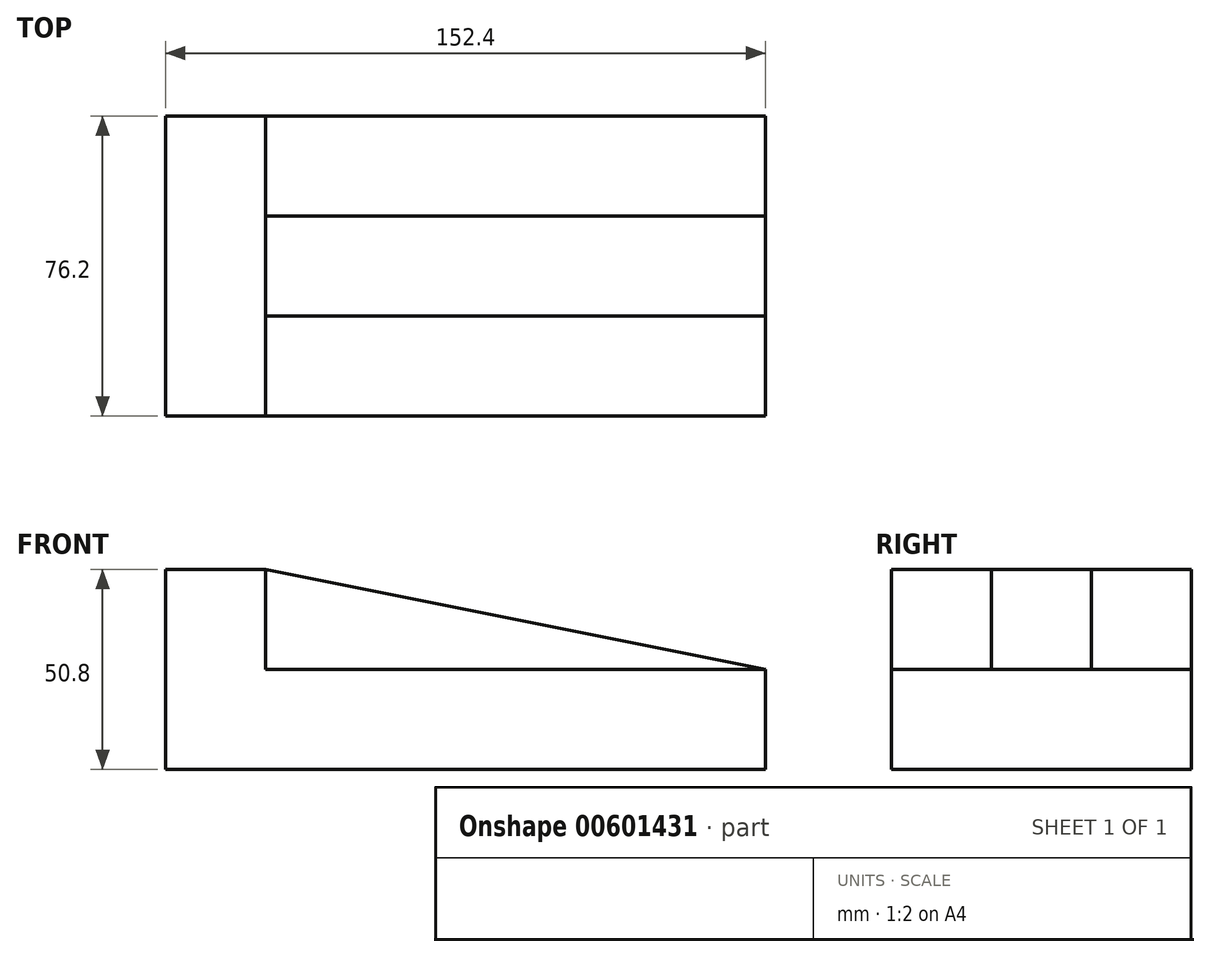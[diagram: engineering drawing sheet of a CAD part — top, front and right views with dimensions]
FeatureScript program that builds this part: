
annotation { "Feature Type Name" : "Feature", "Feature Type Description" : "" }
export const myFeature = defineFeature(function(context is Context, id is Id, definition is map)
    precondition{}
    {
        {
            var Q0;
            Q0=qCreatedBy(makeId("Front.planeOp"),FACE);
            var sketch = newSketch(context, id + "F0", { "sketchPlane" : qUnion([Q0])});
            skLineSegment(sketch, "E0", {"start": v(0, 0) * mm, "end": v(0, 50.8) * mm});
            skLineSegment(sketch, "E1", {"start": v(0, 50.8) * mm, "end": v(25.4, 50.8) * mm});
            skLineSegment(sketch, "E2", {"start": v(25.4, 50.8) * mm, "end": v(152.4, 25.4) * mm});
            skLineSegment(sketch, "E3", {"start": v(152.4, 25.4) * mm, "end": v(152.4, 0) * mm});
            skLineSegment(sketch, "E4", {"start": v(152.4, 0) * mm, "end": v(0, 0) * mm});
            skSolve(sketch);
        }
        {
            var Q0;
            Q0 = qSketchRegion(id + "F0", true);
            extrude(context, id + "F1", {"entities" : qUnion([Q0]), "depth" : 76.2 * mm, "offsetDistance" : 25.4 * mm});
        }
        {
            var Q0;
            Q0=makeQuery(id+"F1.opExtrude","CAP_FACE",FACE,{"disambiguationData":[OSD([sQuery(id+"F0.wireOp",EDGE,"E0"),sQuery(id+"F0.wireOp",EDGE,"E1"),sQuery(id+"F0.wireOp",EDGE,"E2"),sQuery(id+"F0.wireOp",EDGE,"E3"),sQuery(id+"F0.wireOp",EDGE,"E4")])],"isStart":false});
            var sketch = newSketch(context, id + "F2", { "sketchPlane" : qUnion([Q0])});
            skLineSegment(sketch, "E5", {"start": v(25.4, 50.8) * mm, "end": v(25.4, 25.4) * mm});
            skLineSegment(sketch, "E6", {"start": v(25.4, 25.4) * mm, "end": v(152.4, 25.4) * mm});
            skSolve(sketch);
        }
        {
            var Q0;
            Q0 = qSketchRegion(id + "F2", true);
            var Q1;
            Q1=makeQuery(id+"F2.imprint","IMPRINT",FACE,{"disambiguationData":[TD([[makeQuery(id+"F2.imprint","IMPRINT",EDGE,{"derivedFrom":sQuery(id+"F2.wireOp",EDGE,"E5")}),1.0]])]});
            extrude(context, id + "F3", {"entities" : qUnion([Q0, Q1]), "operationType" : NewBodyOperationType.REMOVE, "oppositeDirection" : true, "depth" : 25.4 * mm, "offsetDistance" : 25.4 * mm});
        }
        {
            var Q0;
            Q0=makeQuery(id+"F1.opExtrude","CAP_FACE",FACE,{"disambiguationData":[OSD([sQuery(id+"F0.wireOp",EDGE,"E0"),sQuery(id+"F0.wireOp",EDGE,"E1"),sQuery(id+"F0.wireOp",EDGE,"E2"),sQuery(id+"F0.wireOp",EDGE,"E3"),sQuery(id+"F0.wireOp",EDGE,"E4")])],"isStart":true});
            var sketch = newSketch(context, id + "F4", { "sketchPlane" : qUnion([Q0])});
            skLineSegment(sketch, "E7", {"start": v(-25.4, 50.8) * mm, "end": v(-25.4, 25.4) * mm});
            skLineSegment(sketch, "E8", {"start": v(-25.4, 25.4) * mm, "end": v(-152.4, 25.4) * mm});
            skSolve(sketch);
        }
        {
            var Q0;
            Q0 = qSketchRegion(id + "F4", true);
            var Q1;
            Q1=makeQuery(id+"F4.imprint","IMPRINT",FACE,{"disambiguationData":[TD([[makeQuery(id+"F4.imprint","IMPRINT",EDGE,{"derivedFrom":sQuery(id+"F4.wireOp",EDGE,"E7")}),-1.0]])]});
            extrude(context, id + "F5", {"entities" : qUnion([Q0, Q1]), "operationType" : NewBodyOperationType.REMOVE, "oppositeDirection" : true, "depth" : 25.4 * mm, "offsetDistance" : 25.4 * mm});
        }
    });
